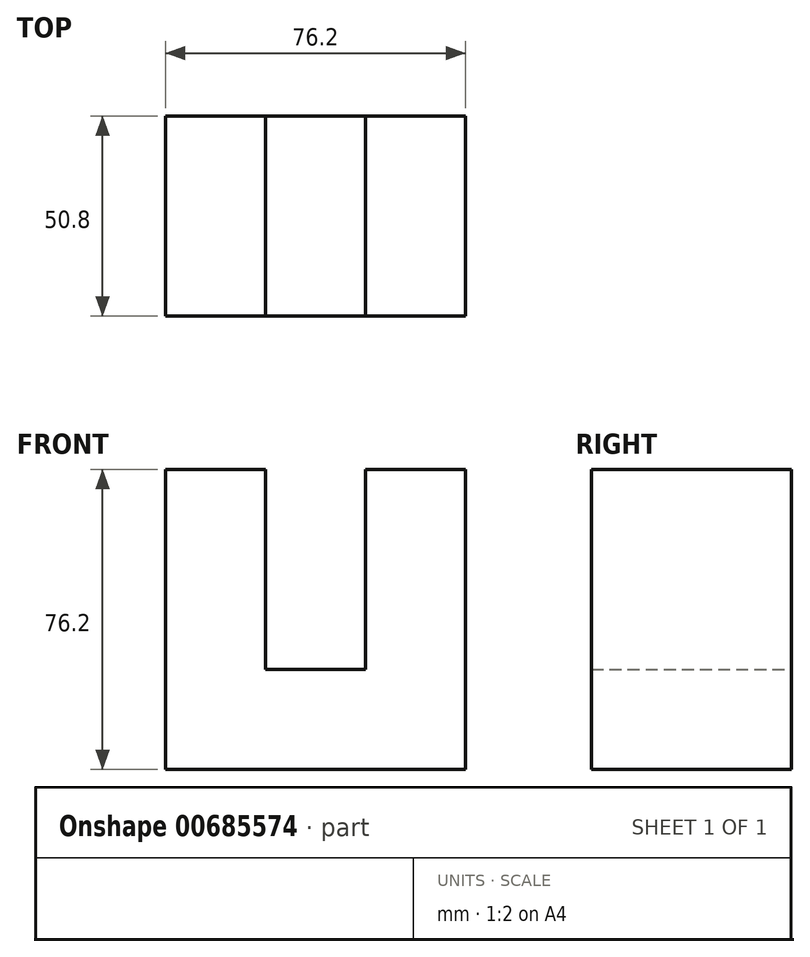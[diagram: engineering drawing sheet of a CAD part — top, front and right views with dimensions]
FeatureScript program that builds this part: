
annotation { "Feature Type Name" : "Feature", "Feature Type Description" : "" }
export const myFeature = defineFeature(function(context is Context, id is Id, definition is map)
    precondition{}
    {
        {
            var Q0;
            Q0=qCreatedBy(makeId("Front.planeOp"),FACE);
            var sketch = newSketch(context, id + "F0", { "sketchPlane" : qUnion([Q0])});
            skLineSegment(sketch, "E0", {"start": v(-9.52, 31.6) * mm, "end": v(-34.92, 31.6) * mm});
            skLineSegment(sketch, "E1", {"start": v(-34.92, 31.6) * mm, "end": v(-34.92, -44.6) * mm});
            skLineSegment(sketch, "E2", {"start": v(-34.92, -44.6) * mm, "end": v(41.28, -44.6) * mm});
            skLineSegment(sketch, "E3", {"start": v(41.28, -44.6) * mm, "end": v(41.28, 31.6) * mm});
            skLineSegment(sketch, "E4", {"start": v(41.28, 31.6) * mm, "end": v(15.88, 31.6) * mm});
            skLineSegment(sketch, "E5", {"start": v(15.88, 31.6) * mm, "end": v(15.88, -19.2) * mm});
            skLineSegment(sketch, "E6", {"start": v(15.88, -19.2) * mm, "end": v(-9.52, -19.2) * mm});
            skLineSegment(sketch, "E7", {"start": v(-9.52, -19.2) * mm, "end": v(-9.52, 31.6) * mm});
            skSolve(sketch);
        }
        {
            var Q0;
            Q0=makeQuery(id+"F0.imprint","IMPRINT",FACE,{"disambiguationData":[TD([[makeQuery(id+"F0.imprint","IMPRINT",EDGE,{"derivedFrom":sQuery(id+"F0.wireOp",EDGE,"E0")}),1.0]])]});
            extrude(context, id + "F1", {"entities" : qUnion([Q0]), "depth" : 50.8 * mm, "offsetDistance" : 25.4 * mm});
        }
    });
